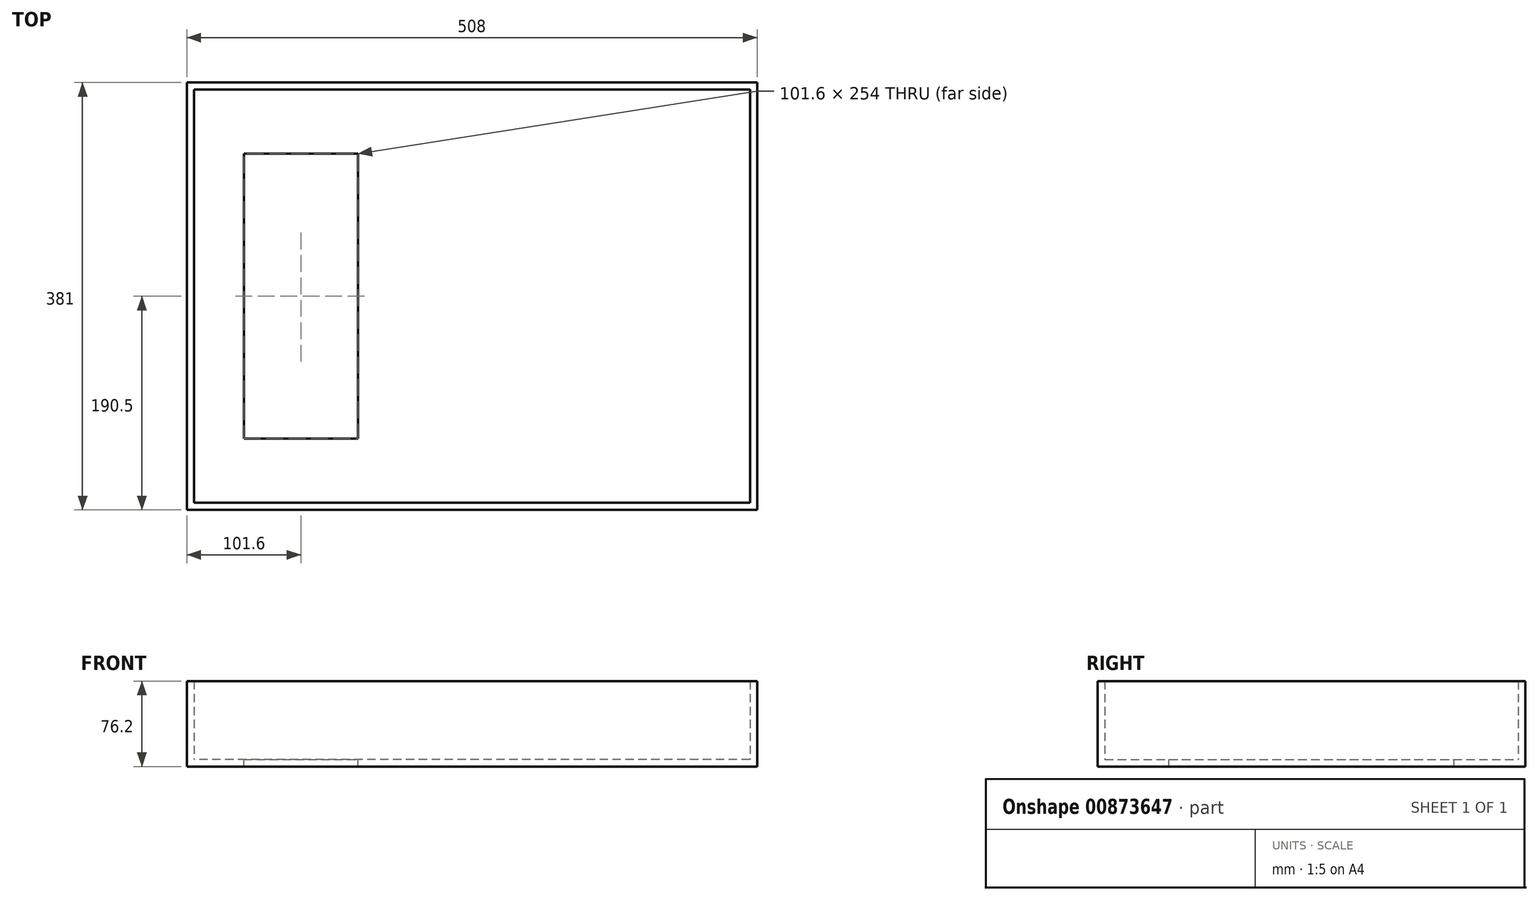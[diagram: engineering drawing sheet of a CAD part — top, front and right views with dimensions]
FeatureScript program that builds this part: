
annotation { "Feature Type Name" : "Feature", "Feature Type Description" : "" }
export const myFeature = defineFeature(function(context is Context, id is Id, definition is map)
    precondition{}
    {
        {
            var Q0;
            Q0=qCreatedBy(makeId("Top.planeOp"),FACE);
            var sketch = newSketch(context, id + "F0", { "sketchPlane" : qUnion([Q0])});
            skLineSegment(sketch, "E0.bottom", {"start": v(254, -190.5) * mm, "end": v(-254, -190.5) * mm});
            skLineSegment(sketch, "E0.top", {"start": v(254, 190.5) * mm, "end": v(-254, 190.5) * mm});
            skLineSegment(sketch, "E0.left", {"start": v(254, -190.5) * mm, "end": v(254, 190.5) * mm});
            skLineSegment(sketch, "E0.right", {"start": v(-254, -190.5) * mm, "end": v(-254, 190.5) * mm});
            skPoint(sketch, "E0.middle", {"position": v(0, 0) * mm});
            skSolve(sketch);
        }
        {
            var Q0;
            Q0=makeQuery(id+"F0.imprint","IMPRINT",FACE,{"disambiguationData":[TD([[makeQuery(id+"F0.imprint","IMPRINT",EDGE,{"derivedFrom":sQuery(id+"F0.wireOp",EDGE,"E0.bottom")}),-1.0]])]});
            extrude(context, id + "F1", {"entities" : qUnion([Q0]), "depth" : 76.2 * mm, "offsetDistance" : 25.4 * mm});
        }
        {
            var Q0;
            Q0=makeQuery(id+"F1.opExtrude","CAP_FACE",FACE,{"disambiguationData":[OSD([sQuery(id+"F0.wireOp",EDGE,"E0.bottom"),sQuery(id+"F0.wireOp",EDGE,"E0.top"),sQuery(id+"F0.wireOp",EDGE,"E0.left"),sQuery(id+"F0.wireOp",EDGE,"E0.right")])],"isStart":false});
            var sketch = newSketch(context, id + "F2", { "sketchPlane" : qUnion([Q0])});
            skLineSegment(sketch, "E1.bottom", {"start": v(-101.6, 127) * mm, "end": v(-203.2, 127) * mm});
            skLineSegment(sketch, "E1.top", {"start": v(-101.6, -127) * mm, "end": v(-203.2, -127) * mm});
            skLineSegment(sketch, "E1.left", {"start": v(-101.6, 127) * mm, "end": v(-101.6, -127) * mm});
            skLineSegment(sketch, "E1.right", {"start": v(-203.2, 127) * mm, "end": v(-203.2, -127) * mm});
            skPoint(sketch, "E1.middle", {"position": v(-152.4, 0) * mm});
            skSolve(sketch);
        }
        {
            var Q0;
            Q0=makeQuery(id+"F2.imprint","IMPRINT",FACE,{"disambiguationData":[TD([[makeQuery(id+"F2.imprint","IMPRINT",EDGE,{"derivedFrom":sQuery(id+"F2.wireOp",EDGE,"E1.bottom")}),1.0]])]});
            extrude(context, id + "F3", {"entities" : qUnion([Q0]), "operationType" : NewBodyOperationType.REMOVE, "endBound" : BoundingType.UP_TO_NEXT, "oppositeDirection" : true, "depth" : 25.4 * mm, "offsetDistance" : 25.4 * mm});
        }
        {
            var Q0;
            Q0=makeQuery(id+"F1.opExtrude","CAP_FACE",FACE,{"disambiguationData":[OSD([sQuery(id+"F0.wireOp",EDGE,"E0.bottom"),sQuery(id+"F0.wireOp",EDGE,"E0.top"),sQuery(id+"F0.wireOp",EDGE,"E0.left"),sQuery(id+"F0.wireOp",EDGE,"E0.right")])],"isStart":false});
            shell(context, id + "F4", {"entities" : qUnion([Q0]), "thickness" : 6.35 * mm});
        }
        {
            var Q0;
            Q0=makeQuery(id+"F1.opExtrude","CAP_FACE",FACE,{"disambiguationData":[OSD([sQuery(id+"F0.wireOp",EDGE,"E0.bottom"),sQuery(id+"F0.wireOp",EDGE,"E0.top"),sQuery(id+"F0.wireOp",EDGE,"E0.left"),sQuery(id+"F0.wireOp",EDGE,"E0.right")])],"isStart":false});
            var sketch = newSketch(context, id + "F5", { "sketchPlane" : qUnion([Q0])});
            skLineSegment(sketch, "E2.bottom", {"start": v(-95.25, 133.35) * mm, "end": v(-209.55, 133.35) * mm});
            skLineSegment(sketch, "E2.top", {"start": v(-95.25, -133.35) * mm, "end": v(-209.55, -133.35) * mm});
            skLineSegment(sketch, "E2.left", {"start": v(-95.25, 133.35) * mm, "end": v(-95.25, -133.35) * mm});
            skLineSegment(sketch, "E2.right", {"start": v(-209.55, 133.35) * mm, "end": v(-209.55, -133.35) * mm});
            skSolve(sketch);
        }
        {
            var Q0;
            Q0=makeQuery(id+"F5.imprint","IMPRINT",FACE,{"disambiguationData":[TD([[makeQuery(id+"F5.imprint","IMPRINT",EDGE,{"derivedFrom":sQuery(id+"F5.wireOp",EDGE,"E2.bottom")}),1.0]])]});
            extrude(context, id + "F6", {"entities" : qUnion([Q0]), "operationType" : NewBodyOperationType.REMOVE, "oppositeDirection" : true, "depth" : 69.85 * mm, "offsetDistance" : 25.4 * mm});
        }
    });
